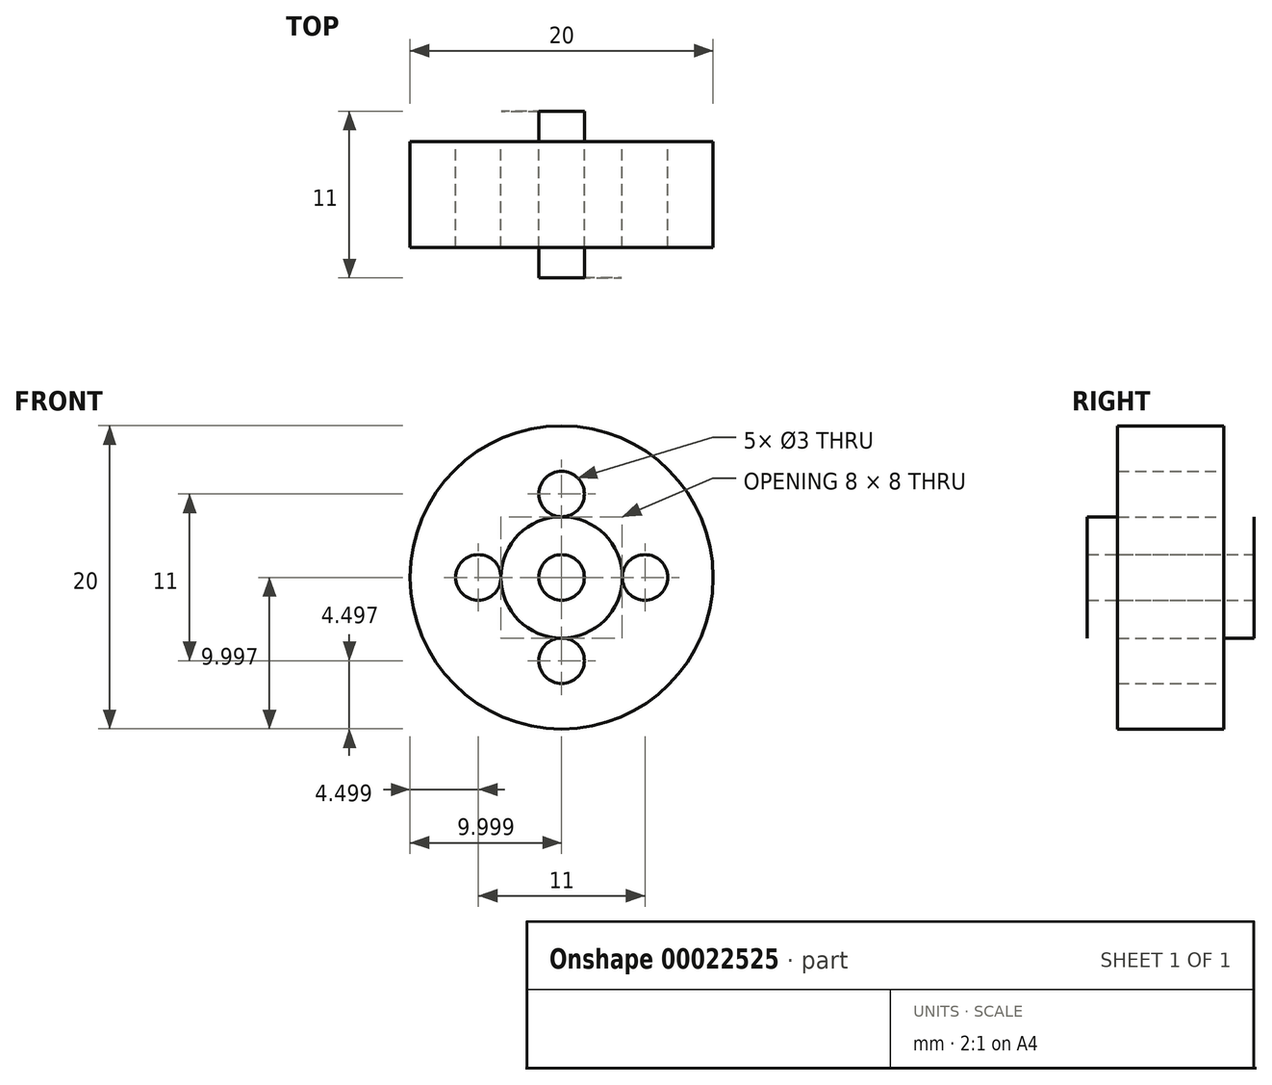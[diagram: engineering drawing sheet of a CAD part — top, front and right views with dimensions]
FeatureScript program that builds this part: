
annotation { "Feature Type Name" : "Feature", "Feature Type Description" : "" }
export const myFeature = defineFeature(function(context is Context, id is Id, definition is map)
    precondition{}
    {
        {
            var Q0;
            Q0=qCreatedBy(makeId("Front.planeOp"),FACE);
            var sketch = newSketch(context, id + "F0", { "sketchPlane" : qUnion([Q0])});
            skCircle(sketch, "E0", {"center": v(-69.7, 4.85) * mm, "radius": 10 * mm});
            skCircle(sketch, "E1", {"center": v(-69.7, 4.85) * mm, "radius": 4 * mm});
            skCircle(sketch, "E2", {"center": v(-69.7, 4.85) * mm, "radius": 1.5 * mm});
            skCircle(sketch, "E3", {"center": v(-69.7, 10.35) * mm, "radius": 1.5 * mm});
            skCircle(sketch, "E4.1.0", {"center": v(-75.2, 4.85) * mm, "radius": 1.5 * mm});
            skCircle(sketch, "E4.2.0", {"center": v(-69.7, -0.65) * mm, "radius": 1.5 * mm});
            skCircle(sketch, "E4.3.0", {"center": v(-64.2, 4.85) * mm, "radius": 1.5 * mm});
            skSolve(sketch);
        }
        {
            var Q0;
            Q0=makeQuery(id+"F0.imprint","IMPRINT",FACE,{"disambiguationData":[TD([[makeQuery(id+"F0.imprint","IMPRINT",EDGE,{"derivedFrom":sQuery(id+"F0.wireOp",EDGE,"E0")}),1.0]])]});
            var Q1;
            Q1=makeQuery(id+"F0.imprint","IMPRINT",FACE,{"disambiguationData":[TD([[makeQuery(id+"F0.imprint","IMPRINT",EDGE,{"derivedFrom":sQuery(id+"F0.wireOp",EDGE,"E2")}),-1.0]])]});
            extrude(context, id + "F1", {"entities" : qUnion([Q0, Q1]), "depth" : 7 * mm});
        }
        {
            var Q0;
            Q0=makeQuery(id+"F0.imprint","IMPRINT",FACE,{"disambiguationData":[TD([[makeQuery(id+"F0.imprint","IMPRINT",EDGE,{"derivedFrom":sQuery(id+"F0.wireOp",EDGE,"E2")}),-1.0]])]});
            extrude(context, id + "F2", {"entities" : qUnion([Q0]), "operationType" : NewBodyOperationType.ADD, "depth" : 9 * mm});
        }
        {
            var Q0;
            Q0=makeQuery(id+"F1.opExtrude","CAP_FACE",FACE,{"disambiguationData":[OSD([sQuery(id+"F0.wireOp",EDGE,"E0"),sQuery(id+"F0.wireOp",EDGE,"E2"),sQuery(id+"F0.wireOp",EDGE,"E3"),sQuery(id+"F0.wireOp",EDGE,"E4.1.0"),sQuery(id+"F0.wireOp",EDGE,"E4.2.0"),sQuery(id+"F0.wireOp",EDGE,"E4.3.0")])],"isStart":true});
            var sketch = newSketch(context, id + "F3", { "sketchPlane" : qUnion([Q0])});
            skCircle(sketch, "E5", {"center": v(69.7, 4.85) * mm, "radius": 4 * mm});
            skSolve(sketch);
        }
        {
            var Q0;
            Q0=makeQuery(id+"F3.imprint","IMPRINT",FACE,{"disambiguationData":[TD([[makeQuery(id+"F3.imprint","IMPRINT",EDGE,{"derivedFrom":makeQuery(id+"F1.opExtrude","CAP_EDGE",EDGE,{"disambiguationData":[OSD([sQuery(id+"F0.wireOp",EDGE,"E2")])],"isStart":true})}),1.0]])]});
            extrude(context, id + "F4", {"entities" : qUnion([Q0]), "operationType" : NewBodyOperationType.ADD, "depth" : 2 * mm});
        }
    });
